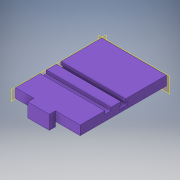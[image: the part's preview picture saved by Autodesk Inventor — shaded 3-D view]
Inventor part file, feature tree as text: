
AUTODESK INVENTOR PART (.ipt)
format: ipt  version: 2018.2 (Build 222227000, 227)  size: 212,992 bytes
history: native  units: in
note: dims shown in document units (in); Inventor stores cm internally (conversion verified against a paired STEP export)
features: extrude x6, sketch x5, mirror x4, split x2, plane x1
ambient origin geometry x8: Origin, YZ Plane, XZ Plane, XY Plane, X Axis, Y Axis, Z Axis, Center Point
bodies: Solid1 (feature_tree)
feature tree (18):
  extrude  "Extrusion1"  Depth=0.375in
  extrude  "Extrusion2"  Depth=0.75in
  mirror  "Mirror1"
  extrude  "Extrusion3"  Depth=7.0in TaperAngle=0.0deg
  extrude  "Extrusion4"  Depth=0.5in TaperAngle=0.0deg
  mirror  "Mirror2"
  extrude  "Extrusion5"  Depth=0.25in
  mirror  "Mirror3"
  extrude  "Extrusion8"  Depth=0.5in
  mirror  "Mirror4"
  split  "Split2"
  plane  "Work Plane1"
  split  "Split3"
  sketch  "Sketch4"  dims[d0=0.375in d1=0.375in]
  sketch  "Sketch6"  dims[d6=2.5in d8=0.75in]
  sketch  "Sketch7"  dims[d9=7.0in d10=14.0in d11=0.0in]
  sketch  "Sketch9"  dims[d12=0.875in d13=0.5in d14=0.0in]
  sketch  "Sketch12"  dims[d16=0.5in d18=0.25in d19=3.5in d20=1.0in d21=0.0in d22=1.75in d23=0.9in d24=1.0in d25=0.5in d26=0.0in d28=0.5in d29=0.25in d30=2.0in d31=0.5in d32=0.0in d46=3.5in d47=0.1875in d48=0.25in d49=0.25in d50=0.344in d51=0.5in d52=0.0in d53=-5.25in]
